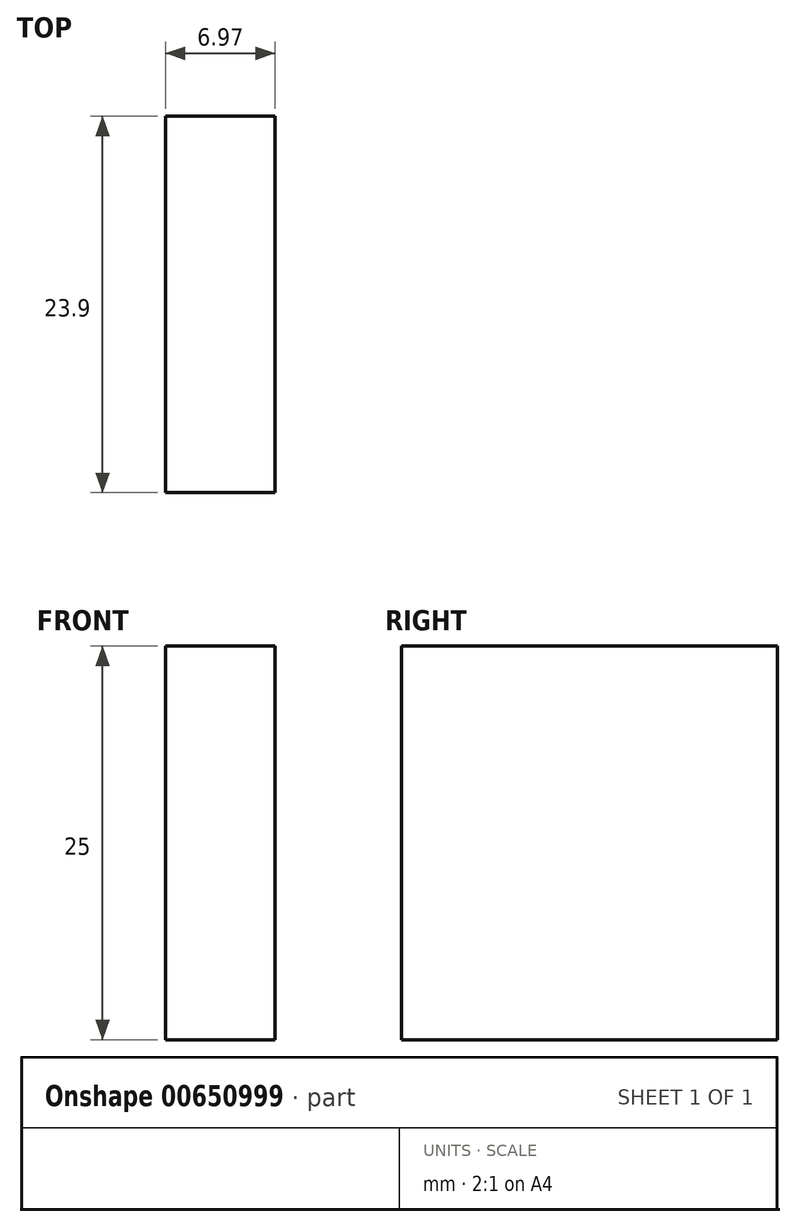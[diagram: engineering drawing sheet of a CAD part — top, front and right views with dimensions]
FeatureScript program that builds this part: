
annotation { "Feature Type Name" : "Feature", "Feature Type Description" : "" }
export const myFeature = defineFeature(function(context is Context, id is Id, definition is map)
    precondition{}
    {
        {
            var Q0;
            Q0=qCreatedBy(makeId("Top.planeOp"),FACE);
            var sketch = newSketch(context, id + "F0", { "sketchPlane" : qUnion([Q0])});
            skLineSegment(sketch, "E0.bottom", {"start": v(-33.55, 40.01) * mm, "end": v(18.35, 40.01) * mm});
            skLineSegment(sketch, "E0.top", {"start": v(-33.55, -8.99) * mm, "end": v(18.35, -8.99) * mm});
            skLineSegment(sketch, "E0.left", {"start": v(-33.55, 40.01) * mm, "end": v(-33.55, -8.99) * mm});
            skLineSegment(sketch, "E0.right", {"start": v(18.35, 40.01) * mm, "end": v(18.35, -8.99) * mm});
            skLineSegment(sketch, "E1.bottom", {"start": v(-33.55, -8.99) * mm, "end": v(36.45, -8.99) * mm});
            skLineSegment(sketch, "E1.top", {"start": v(-33.55, 27.01) * mm, "end": v(36.45, 27.01) * mm});
            skLineSegment(sketch, "E1.left", {"start": v(-33.55, -8.99) * mm, "end": v(-33.55, 27.01) * mm});
            skLineSegment(sketch, "E1.right", {"start": v(36.45, -8.99) * mm, "end": v(36.45, 27.01) * mm});
            skLineSegment(sketch, "E2.bottom", {"start": v(-33.55, -8.99) * mm, "end": v(-11.55, -8.99) * mm});
            skLineSegment(sketch, "E2.top", {"start": v(-33.55, 70.62) * mm, "end": v(-11.55, 70.62) * mm});
            skLineSegment(sketch, "E2.left", {"start": v(-33.55, -8.99) * mm, "end": v(-33.55, 70.62) * mm});
            skLineSegment(sketch, "E2.right", {"start": v(-11.55, -8.99) * mm, "end": v(-11.55, 70.62) * mm});
            skLineSegment(sketch, "E3.bottom", {"start": v(-33.55, -8.99) * mm, "end": v(-4.58, -8.99) * mm});
            skLineSegment(sketch, "E3.top", {"start": v(-33.55, 14.91) * mm, "end": v(-4.58, 14.91) * mm});
            skLineSegment(sketch, "E3.left", {"start": v(-33.55, -8.99) * mm, "end": v(-33.55, 14.91) * mm});
            skLineSegment(sketch, "E3.right", {"start": v(-4.58, -8.99) * mm, "end": v(-4.58, 14.91) * mm});
            skSolve(sketch);
        }
        {
            var Q0;
            {var subQ5=sQuery(id+"F0.wireOp",EDGE,"E3.left");Q0=makeQuery(id+"F0.imprint","IMPRINT",FACE,{"disambiguationData":[TD([[makeQuery(id+"F0.imprint","IMPRINT",EDGE,{"derivedFrom":subQ5}),-1.0]])]});}
            var Q1;
            {var subQ5=sQuery(id+"F0.wireOp",EDGE,"E3.right");Q1=makeQuery(id+"F0.imprint","IMPRINT",FACE,{"disambiguationData":[TD([[makeQuery(id+"F0.imprint","IMPRINT",EDGE,{"derivedFrom":subQ5}),1.0]])]});}
            extrude(context, id + "F1", {"entities" : qUnion([Q0, Q1]), "depth" : 25 * mm, "offsetDistance" : 25 * mm});
        }
    });
